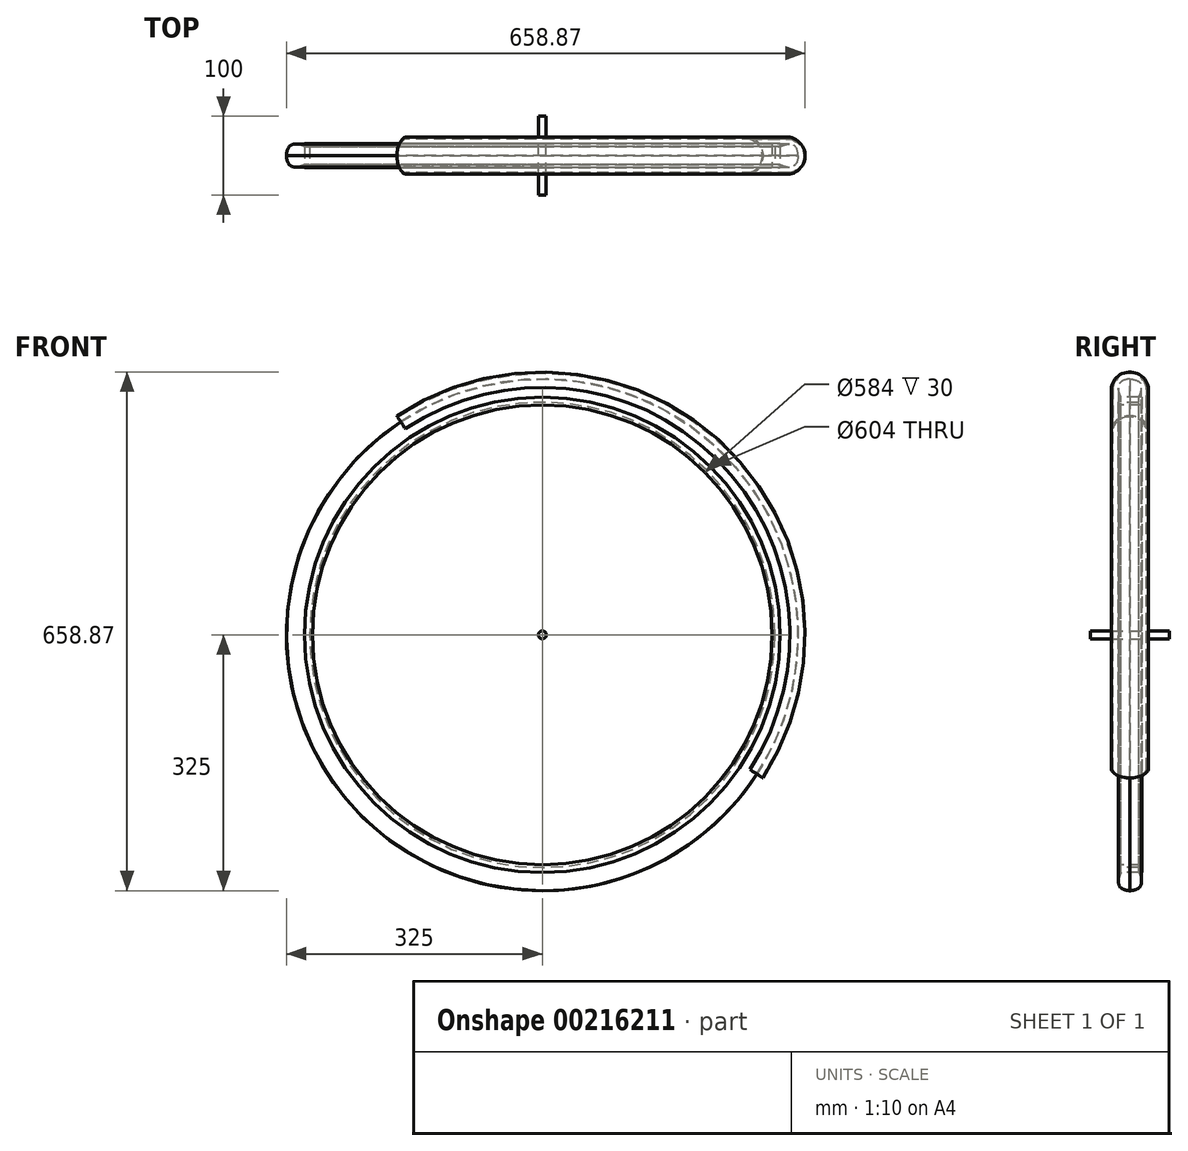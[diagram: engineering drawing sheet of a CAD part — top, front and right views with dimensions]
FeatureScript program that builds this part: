
annotation { "Feature Type Name" : "Feature", "Feature Type Description" : "" }
export const myFeature = defineFeature(function(context is Context, id is Id, definition is map)
    precondition{}
    {
        {
            var Q0;
            Q0=qCreatedBy(makeId("Top.planeOp"),FACE);
            var sketch = newSketch(context, id + "F0", { "sketchPlane" : qUnion([Q0])});
            skLineSegment(sketch, "E0", {"start": v(0, 0) * mm, "end": v(305, 0) * mm, "construction": true});
            skCircle(sketch, "E1", {"center": v(305, 0) * mm, "radius": 20 * mm});
            skLineSegment(sketch, "E2", {"start": v(0, 0) * mm, "end": v(0, 35.05) * mm, "construction": true});
            skSolve(sketch);
        }
        {
            var Q0;
            Q0=qCreatedBy(makeId("Front.planeOp"),FACE);
            var sketch = newSketch(context, id + "F1", { "sketchPlane" : qUnion([Q0])});
            skCircle(sketch, "E3", {"center": v(0, 0) * mm, "radius": 5 * mm});
            skSolve(sketch);
        }
        {
            var Q0;
            Q0=makeQuery(id+"F1.imprint","IMPRINT",FACE,{"disambiguationData":[TD([[makeQuery(id+"F1.imprint","IMPRINT",EDGE,{"derivedFrom":sQuery(id+"F1.wireOp",EDGE,"E3")}),1.0]])]});
            extrude(context, id + "F2", {"entities" : qUnion([Q0]), "depth" : 100 * mm, "symmetric" : true});
        }
        {
            var Q0;
            Q0=qCreatedBy(makeId("Right.planeOp"),FACE);
            var sketch = newSketch(context, id + "F3", { "sketchPlane" : qUnion([Q0])});
            skLineSegment(sketch, "E4", {"start": v(0, 0) * mm, "end": v(0, 292) * mm, "construction": true});
            skLineSegment(sketch, "E5", {"start": v(0, 292) * mm, "end": v(15, 292) * mm});
            skLineSegment(sketch, "E6", {"start": v(15, 292) * mm, "end": v(15, 302) * mm});
            skLineSegment(sketch, "E7.MirrorCS", {"start": v(0, 292) * mm, "end": v(-15, 292) * mm});
            skLineSegment(sketch, "E8.MirrorCS", {"start": v(-15, 292) * mm, "end": v(-15, 302) * mm});
            skLineSegment(sketch, "E9", {"start": v(15, 302) * mm, "end": v(11.34, 302) * mm});
            skLineSegment(sketch, "E10", {"start": v(11.34, 302) * mm, "end": v(11.34, 295.48) * mm});
            skLineSegment(sketch, "E11", {"start": v(11.34, 295.48) * mm, "end": v(-11.38, 295.48) * mm});
            skLineSegment(sketch, "E12", {"start": v(-11.38, 295.48) * mm, "end": v(-11.38, 302) * mm});
            skLineSegment(sketch, "E13", {"start": v(-15, 302) * mm, "end": v(-11.38, 302) * mm});
            skLineSegment(sketch, "E14", {"start": v(0, 0) * mm, "end": v(0, 325) * mm, "construction": true});
            skFitSpline(sketch, "E15", {"points": [v(11.34, 302) * mm, v(14.56, 314.38) * mm, v(10.07, 322.53) * mm, v(0, 325) * mm], "startDerivative": vector(15.91, 33.93) * mm, "endDerivative": vector(-13.6, -0.52) * mm});
            skFitSpline(sketch, "E16.MirrorCS", {"points": [v(-11.34, 302) * mm, v(-14.56, 314.38) * mm, v(-10.07, 322.53) * mm, v(0, 325) * mm], "startDerivative": vector(-15.91, 33.93) * mm, "endDerivative": vector(13.6, -0.52) * mm});
            skLineSegment(sketch, "E17", {"start": v(11.34, 302) * mm, "end": v(-11.34, 302) * mm});
            skArc(sketch, "E18", {"start": v(23.45, 314.38) * mm, "mid": v(-0.15, 333.87) * mm, "end": v(-23.76, 314.38) * mm});
            skArc(sketch, "E19", {"start": v(20.69, 314.38) * mm, "mid": v(-0.47, 332.35) * mm, "end": v(-21.63, 314.38) * mm});
            skLineSegment(sketch, "E20", {"start": v(23.45, 314.38) * mm, "end": v(20.69, 314.38) * mm});
            skLineSegment(sketch, "E21", {"start": v(-21.63, 314.38) * mm, "end": v(-23.76, 314.38) * mm});
            skSolve(sketch);
        }
        {
            var Q0;
            Q0=makeQuery(id+"F3.imprint","IMPRINT",FACE,{"disambiguationData":[TD([[makeQuery(id+"F3.imprint","IMPRINT",EDGE,{"derivedFrom":sQuery(id+"F3.wireOp",EDGE,"E5")}),1.0]])]});
            var Q1;
            Q1=sQuery(id+"F0.wireOp",EDGE,"E2");
            revolve(context, id + "F4", {"entities" : qUnion([Q0]), "axis" : qUnion([Q1]), "revolveType" : RevolveType.FULL});
        }
        {
            var Q0;
            Q0=makeQuery(id+"F3.imprint","IMPRINT",FACE,{"disambiguationData":[TD([[makeQuery(id+"F3.imprint","IMPRINT",EDGE,{"derivedFrom":sQuery(id+"F3.wireOp",EDGE,"E15")}),1.0]])]});
            var Q1;
            Q1=sQuery(id+"F0.wireOp",EDGE,"E2");
            revolve(context, id + "F5", {"entities" : qUnion([Q0]), "axis" : qUnion([Q1]), "revolveType" : RevolveType.FULL});
        }
        {
            var Q0;
            Q0=makeQuery(id+"F3.imprint","IMPRINT",FACE,{"disambiguationData":[TD([[makeQuery(id+"F3.imprint","IMPRINT",EDGE,{"derivedFrom":sQuery(id+"F3.wireOp",EDGE,"E18")}),1.0]])]});
            var Q1;
            Q1=sQuery(id+"F0.wireOp",EDGE,"E2");
            revolve(context, id + "F6", {"entities" : qUnion([Q0]), "axis" : qUnion([Q1]), "revolveType" : RevolveType.TWO_DIRECTIONS, "angle" : 122.97 * degree, "angleBack" : 326.4 * degree});
        }
        {
            var Q0;
            Q0=qCreatedBy(makeId("Front.planeOp"),FACE);
            var sketch = newSketch(context, id + "F7", { "sketchPlane" : qUnion([Q0])});
            skLineSegment(sketch, "E22", {"start": v(0, 0) * mm, "end": v(-118.38, 387.2) * mm, "construction": true});
            skLineSegment(sketch, "E23.0", {"start": v(-45.37, -13.87) * mm, "end": v(-163.75, 373.32) * mm, "construction": true});
            skSolve(sketch);
        }
        {
            var Q0;
            Q0=sQuery(id+"F7.wireOp",EDGE,"E22");
            cPlane(context, id + "F8", {"entities" : qUnion([Q0]), "cplaneType" : CPlaneType.LINE_ANGLE, "offset" : 152.4 * mm, "angle" : 0 * degree, "width" : 152.4 * mm, "height" : 152.4 * mm});
        }
        {
            var Q0;
            Q0=qCreatedBy(id+"F8.planeOp",FACE);
            var sketch = newSketch(context, id + "F9", { "sketchPlane" : qUnion([Q0])});
            skLineSegment(sketch, "E24", {"start": v(17.08, 296.48) * mm, "end": v(36.3, 296.48) * mm});
            skLineSegment(sketch, "E25", {"start": v(36.3, 296.48) * mm, "end": v(36.3, 353.48) * mm});
            skLineSegment(sketch, "E26", {"start": v(36.3, 353.48) * mm, "end": v(0, 353.48) * mm});
            skSolve(sketch);
        }
        {
            var Q0;
            Q0=sQuery(id+"F9.wireOp",VERTEX,"E26.end");
            var Q1;
            Q1=sQuery(id+"F7.wireOp",EDGE,"E22");
            cPlane(context, id + "F10", {"entities" : qUnion([Q0, Q1]), "cplaneType" : CPlaneType.LINE_POINT, "offset" : 152.4 * mm, "width" : 152.4 * mm, "height" : 152.4 * mm});
        }
    });
